# Revit family: Storage-Teknion-EMT1_Single_Tower-R2016
name_source: partatom
category: Furniture
revit_build: Autodesk Revit 2018 (Build: 20190510_1515(x64)
units: mm (PartAtom-declared; Revit-internal decimal feet)

## family parameters
Always vertical = Yes
Cut with Voids When Loaded = No
OmniClass Number = 23.40.20.00
OmniClass Title = General Furniture and Specialties
Room Calculation Point = No
Shared = Yes
Work Plane-Based = No

## types (5) — shared parameters
Assembly Code = E2020200
Double Drawers = Yes
Manufacturer = Teknion
Manufacturer Fax = 416.661.4586
Part Number = EMT1
Product Documentation Link = https://assets.teknion.com
Product Line = Emote
Product Page URL = https://www.teknion.com
Series = Emote
Sustainability Data = https://www.teknion.com
URL = www.teknion.com
Unit Weight URL = http://www.teknion.com
Warranty = http://www.teknion.com

## per-type parameters (varying)
| type | Bottom Cabinet Horizontal Pull Visibility | Bottom Cabinet Visibility | Bottom Drawer Offset | Bottom Drawer Visibility | Bottom Shelf Height Offset | Bottom Shelf Visibility | Coat | Description | Model | Not Open | Open | Second Shelf Visibility | Third Shelf Visibility | Top Handle Visiblity | Two Drawer Divider Cut Depth |
| Open | No | No | 20.7 " | No | 20.7 " | Yes | No | Emote Single Tower, Open, 15" Width, 62.3" Height | EMT1OP1562_ | No | Yes | Yes | Yes | No | 0.5 " |
| Lower Drawer | Yes | Yes | 24.95 " | Yes | 24.95 " | Yes | No | Emote Single Tower, Lower Drawer, 15" Width, 62.3" Height | EMT1LD1562_ | Yes | No | Yes | Yes | No | 0.5 " |
| Lower Drawer/Closed Upper | Yes | Yes | 58.746 " | Yes | 24.95 " | Yes | No | Emote Single Tower, Lower Drawer/Closed Upper, 15" Width, 62.3" Height | EMT1DC1562_ | Yes | No | No | No | Yes | 2.07 " |
| Closed Full | No | Yes | 58.746 " | Yes | 24.95 " | No | No | Emote Single Tower, Closed Full, 15" Width, 62.3" Height | EMT1FC1562_ | Yes | No | No | No | Yes | 0.5 " |
| Coat | No | Yes | 58.746 " | Yes | 24.95 " | No | Yes | Emote Single Tower, Coat, 15" Width, 62.3" Height | EMT1CT1562_ | Yes | No | No | No | Yes | 0.5 " |

type visibility flags (boolean, named after types; folded from table):
- Open: Yes: (none)
- Lower Drawer: Yes: Lower Drawer
- Lower Drawer/Closed Upper: Yes: Lower Drawer/Closed Upper
- Closed Full: Yes: Closed Full
- Coat: Yes: (none)

## geometry (parser evidence)
native form markers: Blend x47, Sweep x2
no freeform markers — native parametric forms only
